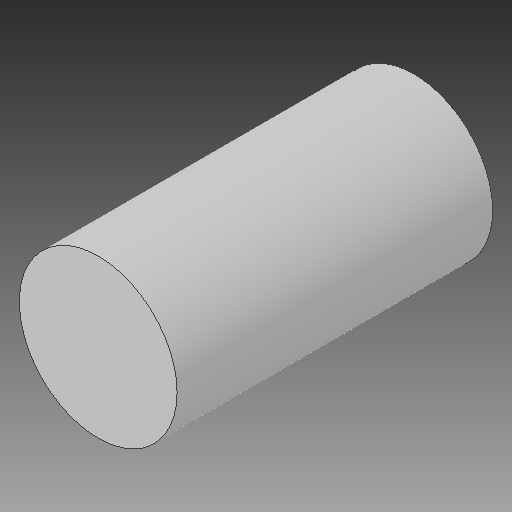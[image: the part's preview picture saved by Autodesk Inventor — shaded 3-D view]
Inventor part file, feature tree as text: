
AUTODESK INVENTOR PART (.ipt)
format: ipt  version: 2018 (Build 220112000, 112)  size: 90,112 bytes
history: native  units: in
note: dims shown in document units (in); Inventor stores cm internally (conversion verified against a paired STEP export)
features: extrude x1, sketch x1
ambient origin geometry x8: Origin, YZ Plane, XZ Plane, XY Plane, X Axis, Y Axis, Z Axis, Center Point
bodies: Solid1 (feature_tree)
feature tree (2):
  extrude  "Extrusion1"  Depth=0.5in TaperAngle=0.0deg
  sketch  "Sketch1"  dims[d0=0.25in d1=0.5in d2=0.0in]
